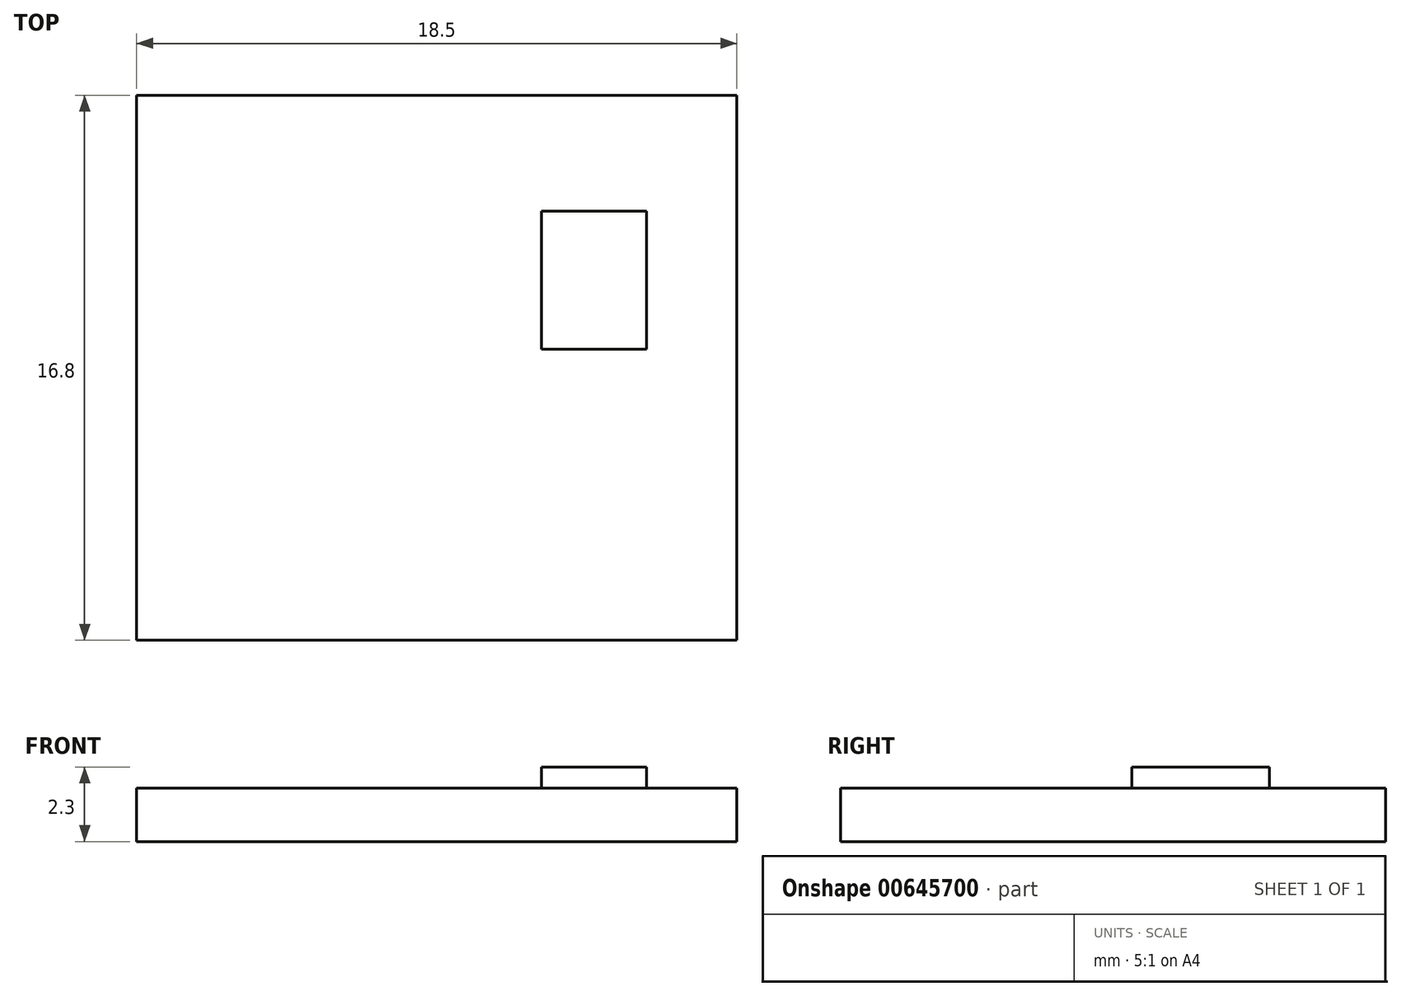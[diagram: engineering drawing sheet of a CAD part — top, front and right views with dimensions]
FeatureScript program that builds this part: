
annotation { "Feature Type Name" : "Feature", "Feature Type Description" : "" }
export const myFeature = defineFeature(function(context is Context, id is Id, definition is map)
    precondition{}
    {
        {
            var Q0;
            Q0=qCreatedBy(makeId("Top.planeOp"),FACE);
            var sketch = newSketch(context, id + "F0", { "sketchPlane" : qUnion([Q0])});
            skLineSegment(sketch, "E0", {"start": v(4.4, 15.81) * mm, "end": v(4.4, -30.02) * mm, "construction": true});
            skLineSegment(sketch, "E1", {"start": v(-20.7, 5.7) * mm, "end": v(26.39, 5.7) * mm, "construction": true});
            skLineSegment(sketch, "E2", {"start": v(-14.1, 17.65) * mm, "end": v(-14.1, -24.47) * mm, "construction": true});
            skLineSegment(sketch, "E3", {"start": v(-29.13, -11.1) * mm, "end": v(19.27, -11.1) * mm, "construction": true});
            skLineSegment(sketch, "E4.bottom", {"start": v(-1.62, 2.12) * mm, "end": v(1.62, 2.12) * mm});
            skLineSegment(sketch, "E4.top", {"start": v(-1.62, -2.12) * mm, "end": v(1.62, -2.12) * mm});
            skLineSegment(sketch, "E4.left", {"start": v(-1.62, 2.12) * mm, "end": v(-1.62, -2.12) * mm});
            skLineSegment(sketch, "E4.right", {"start": v(1.62, 2.12) * mm, "end": v(1.62, -2.12) * mm});
            skPoint(sketch, "E4.middle", {"position": v(0, 0) * mm});
            skLineSegment(sketch, "E5.bottom", {"start": v(-14.1, 5.7) * mm, "end": v(4.4, 5.7) * mm});
            skLineSegment(sketch, "E5.top", {"start": v(-14.1, -11.1) * mm, "end": v(4.4, -11.1) * mm});
            skLineSegment(sketch, "E5.left", {"start": v(-14.1, 5.7) * mm, "end": v(-14.1, -11.1) * mm});
            skLineSegment(sketch, "E5.right", {"start": v(4.4, 5.7) * mm, "end": v(4.4, -11.1) * mm});
            skSolve(sketch);
        }
        {
            var Q0;
            Q0=makeQuery(id+"F0.imprint","IMPRINT",FACE,{"disambiguationData":[TD([[makeQuery(id+"F0.imprint","IMPRINT",EDGE,{"derivedFrom":sQuery(id+"F0.wireOp",EDGE,"E4.bottom")}),-1.0]])]});
            extrude(context, id + "F1", {"entities" : qUnion([Q0]), "depth" : 2.3 * mm, "offsetDistance" : 25 * mm});
        }
        {
            var Q0;
            Q0=makeQuery(id+"F0.imprint","IMPRINT",FACE,{"disambiguationData":[TD([[makeQuery(id+"F0.imprint","IMPRINT",EDGE,{"derivedFrom":sQuery(id+"F0.wireOp",EDGE,"E4.bottom")}),1.0]])]});
            extrude(context, id + "F2", {"entities" : qUnion([Q0]), "operationType" : NewBodyOperationType.ADD, "depth" : 1.65 * mm, "offsetDistance" : 25 * mm});
        }
    });
